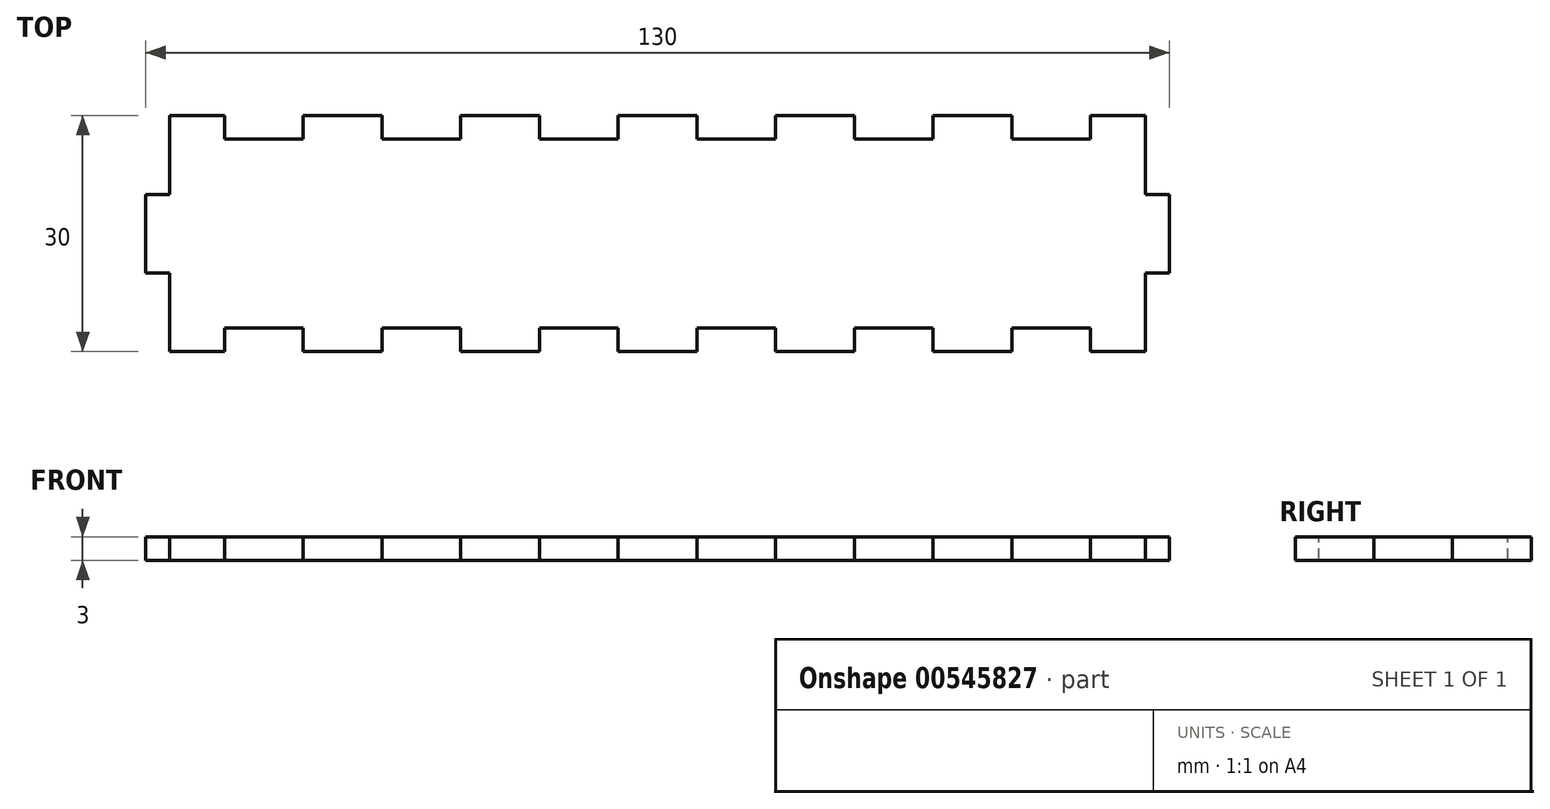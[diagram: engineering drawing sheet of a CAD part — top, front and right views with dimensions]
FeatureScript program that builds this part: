
annotation { "Feature Type Name" : "Feature", "Feature Type Description" : "" }
export const myFeature = defineFeature(function(context is Context, id is Id, definition is map)
    precondition{}
    {
        {
            var Q0;
            Q0=qCreatedBy(makeId("Top.planeOp"),FACE);
            var sketch = newSketch(context, id + "F0", { "sketchPlane" : qUnion([Q0])});
            skLineSegment(sketch, "E0.bottom", {"start": v(65, -15) * mm, "end": v(-65, -15) * mm});
            skLineSegment(sketch, "E0.top", {"start": v(65, 15) * mm, "end": v(-65, 15) * mm});
            skLineSegment(sketch, "E0.left", {"start": v(65, -15) * mm, "end": v(65, 15) * mm});
            skLineSegment(sketch, "E0.right", {"start": v(-65, -15) * mm, "end": v(-65, 15) * mm});
            skPoint(sketch, "E0.middle", {"position": v(0, 0) * mm});
            skSolve(sketch);
        }
        {
            var Q0;
            Q0=makeQuery(id+"F0.imprint","IMPRINT",FACE,{"disambiguationData":[TD([[makeQuery(id+"F0.imprint","IMPRINT",EDGE,{"derivedFrom":sQuery(id+"F0.wireOp",EDGE,"E0.bottom")}),-1.0]])]});
            var sketch = newSketch(context, id + "F1", { "sketchPlane" : qUnion([Q0])});
            skLineSegment(sketch, "E1.bottom", {"start": v(65, -15) * mm, "end": v(62, -15) * mm});
            skLineSegment(sketch, "E1.top", {"start": v(65, -5) * mm, "end": v(62, -5) * mm});
            skLineSegment(sketch, "E1.left", {"start": v(65, -15) * mm, "end": v(65, -5) * mm});
            skLineSegment(sketch, "E1.right", {"start": v(62, -15) * mm, "end": v(62, -5) * mm});
            skLineSegment(sketch, "E2.0.1.0", {"start": v(62, 5) * mm, "end": v(62, 15) * mm});
            skLineSegment(sketch, "E2.0.1.1", {"start": v(65, 5) * mm, "end": v(65, 15) * mm});
            skLineSegment(sketch, "E2.0.1.2", {"start": v(65, 15) * mm, "end": v(62, 15) * mm});
            skLineSegment(sketch, "E2.0.1.3", {"start": v(65, 5) * mm, "end": v(62, 5) * mm});
            skLineSegment(sketch, "E2.0.2.0", {"start": v(62, 25) * mm, "end": v(62, 35) * mm});
            skLineSegment(sketch, "E2.0.2.1", {"start": v(65, 25) * mm, "end": v(65, 35) * mm});
            skLineSegment(sketch, "E2.0.2.2", {"start": v(65, 35) * mm, "end": v(62, 35) * mm});
            skLineSegment(sketch, "E2.0.2.3", {"start": v(65, 25) * mm, "end": v(62, 25) * mm});
            skLineSegment(sketch, "E2.0.3.0", {"start": v(62, 45) * mm, "end": v(62, 55) * mm});
            skLineSegment(sketch, "E2.0.3.1", {"start": v(65, 45) * mm, "end": v(65, 55) * mm});
            skLineSegment(sketch, "E2.0.3.2", {"start": v(65, 55) * mm, "end": v(62, 55) * mm});
            skLineSegment(sketch, "E2.0.3.3", {"start": v(65, 45) * mm, "end": v(62, 45) * mm});
            skLineSegment(sketch, "E2.0.4.0", {"start": v(62, 65) * mm, "end": v(62, 75) * mm});
            skLineSegment(sketch, "E2.0.4.1", {"start": v(65, 65) * mm, "end": v(65, 75) * mm});
            skLineSegment(sketch, "E2.0.4.2", {"start": v(65, 75) * mm, "end": v(62, 75) * mm});
            skLineSegment(sketch, "E2.0.4.3", {"start": v(65, 65) * mm, "end": v(62, 65) * mm});
            skLineSegment(sketch, "E2.0.5.0", {"start": v(62, 85) * mm, "end": v(62, 95) * mm});
            skLineSegment(sketch, "E2.0.5.1", {"start": v(65, 85) * mm, "end": v(65, 95) * mm});
            skLineSegment(sketch, "E2.0.5.2", {"start": v(65, 95) * mm, "end": v(62, 95) * mm});
            skLineSegment(sketch, "E2.0.5.3", {"start": v(65, 85) * mm, "end": v(62, 85) * mm});
            skLineSegment(sketch, "E2.direction1", {"start": v(62, -15) * mm, "end": v(87, -15) * mm, "construction": true});
            skLineSegment(sketch, "E2.direction2", {"start": v(62, -15) * mm, "end": v(62, 5) * mm, "construction": true});
            skLineSegment(sketch, "E3", {"start": v(0, -56.46) * mm, "end": v(0, 57.33) * mm, "construction": true});
            skLineSegment(sketch, "E4.MirrorCS", {"start": v(-62, -15) * mm, "end": v(-62, 5) * mm, "construction": true});
            skLineSegment(sketch, "E5.MirrorCS", {"start": v(-62, -15) * mm, "end": v(-62, -5) * mm});
            skLineSegment(sketch, "E6.MirrorCS", {"start": v(-65, 65) * mm, "end": v(-65, 75) * mm});
            skLineSegment(sketch, "E7.MirrorCS", {"start": v(-62, 45) * mm, "end": v(-62, 55) * mm});
            skLineSegment(sketch, "E8.MirrorCS", {"start": v(-65, 25) * mm, "end": v(-62, 25) * mm});
            skLineSegment(sketch, "E9.MirrorCS", {"start": v(-65, 35) * mm, "end": v(-62, 35) * mm});
            skLineSegment(sketch, "E10.MirrorCS", {"start": v(-65, 65) * mm, "end": v(-62, 65) * mm});
            skLineSegment(sketch, "E11.MirrorCS", {"start": v(-65, 25) * mm, "end": v(-65, 35) * mm});
            skLineSegment(sketch, "E12.MirrorCS", {"start": v(-62, 25) * mm, "end": v(-62, 35) * mm});
            skLineSegment(sketch, "E13.MirrorCS", {"start": v(-65, 85) * mm, "end": v(-65, 95) * mm});
            skLineSegment(sketch, "E14.MirrorCS", {"start": v(-65, 5) * mm, "end": v(-62, 5) * mm});
            skLineSegment(sketch, "E15.MirrorCS", {"start": v(-65, 85) * mm, "end": v(-62, 85) * mm});
            skLineSegment(sketch, "E16.MirrorCS", {"start": v(-65, 95) * mm, "end": v(-62, 95) * mm});
            skLineSegment(sketch, "E17.MirrorCS", {"start": v(-62, 85) * mm, "end": v(-62, 95) * mm});
            skLineSegment(sketch, "E18.MirrorCS", {"start": v(-62, 65) * mm, "end": v(-62, 75) * mm});
            skLineSegment(sketch, "E19.MirrorCS", {"start": v(-65, 45) * mm, "end": v(-65, 55) * mm});
            skLineSegment(sketch, "E20.MirrorCS", {"start": v(-65, 55) * mm, "end": v(-62, 55) * mm});
            skLineSegment(sketch, "E21.MirrorCS", {"start": v(-65, 45) * mm, "end": v(-62, 45) * mm});
            skLineSegment(sketch, "E22.MirrorCS", {"start": v(-65, -15) * mm, "end": v(-62, -15) * mm});
            skLineSegment(sketch, "E23.MirrorCS", {"start": v(-65, -15) * mm, "end": v(-65, -5) * mm});
            skLineSegment(sketch, "E24.MirrorCS", {"start": v(-62, 5) * mm, "end": v(-62, 15) * mm});
            skLineSegment(sketch, "E25.MirrorCS", {"start": v(-65, 5) * mm, "end": v(-65, 15) * mm});
            skLineSegment(sketch, "E26.MirrorCS", {"start": v(-65, 15) * mm, "end": v(-62, 15) * mm});
            skLineSegment(sketch, "E27.MirrorCS", {"start": v(-65, 75) * mm, "end": v(-62, 75) * mm});
            skLineSegment(sketch, "E28.MirrorCS", {"start": v(-65, -5) * mm, "end": v(-62, -5) * mm});
            skSolve(sketch);
        }
        {
            var Q0;
            Q0=qSketchRegion(id+"F0",true);
            extrude(context, id + "F2", {"entities" : qUnion([Q0]), "depth" : 3 * mm, "offsetDistance" : 25 * mm});
        }
        {
            var Q0;
            Q0=qSketchRegion(id+"F1",true);
            extrude(context, id + "F3", {"entities" : qUnion([Q0]), "operationType" : NewBodyOperationType.REMOVE, "depth" : 25 * mm, "offsetDistance" : 25 * mm});
        }
        {
            var Q0;
            Q0=makeQuery(id+"F2.opExtrude","CAP_FACE",FACE,{"disambiguationData":[OSD([sQuery(id+"F0.wireOp",EDGE,"E0.bottom"),sQuery(id+"F0.wireOp",EDGE,"E0.top"),sQuery(id+"F0.wireOp",EDGE,"E0.left"),sQuery(id+"F0.wireOp",EDGE,"E0.right")])],"isStart":false});
            var sketch = newSketch(context, id + "F4", { "sketchPlane" : qUnion([Q0])});
            skPoint(sketch, "E29.firstSnap0", {"position": v(0, -15) * mm});
            skLineSegment(sketch, "E29.bottom", {"start": v(-55, -15) * mm, "end": v(-45, -15) * mm});
            skLineSegment(sketch, "E29.top", {"start": v(-55, -12) * mm, "end": v(-45, -12) * mm});
            skLineSegment(sketch, "E29.left", {"start": v(-55, -15) * mm, "end": v(-55, -12) * mm});
            skLineSegment(sketch, "E29.right", {"start": v(-45, -15) * mm, "end": v(-45, -12) * mm});
            skLineSegment(sketch, "E30.1.0.0", {"start": v(-35, -12) * mm, "end": v(-25, -12) * mm});
            skLineSegment(sketch, "E30.1.0.1", {"start": v(-35, -15) * mm, "end": v(-25, -15) * mm});
            skLineSegment(sketch, "E30.1.0.2", {"start": v(-25, -15) * mm, "end": v(-25, -12) * mm});
            skLineSegment(sketch, "E30.1.0.3", {"start": v(-35, -15) * mm, "end": v(-35, -12) * mm});
            skLineSegment(sketch, "E30.2.0.0", {"start": v(-15, -12) * mm, "end": v(-5, -12) * mm});
            skLineSegment(sketch, "E30.2.0.1", {"start": v(-15, -15) * mm, "end": v(-5, -15) * mm});
            skLineSegment(sketch, "E30.2.0.2", {"start": v(-5, -15) * mm, "end": v(-5, -12) * mm});
            skLineSegment(sketch, "E30.2.0.3", {"start": v(-15, -15) * mm, "end": v(-15, -12) * mm});
            skLineSegment(sketch, "E30.3.0.0", {"start": v(5, -12) * mm, "end": v(15, -12) * mm});
            skLineSegment(sketch, "E30.3.0.1", {"start": v(5, -15) * mm, "end": v(15, -15) * mm});
            skLineSegment(sketch, "E30.3.0.2", {"start": v(15, -15) * mm, "end": v(15, -12) * mm});
            skLineSegment(sketch, "E30.3.0.3", {"start": v(5, -15) * mm, "end": v(5, -12) * mm});
            skLineSegment(sketch, "E30.4.0.0", {"start": v(25, -12) * mm, "end": v(35, -12) * mm});
            skLineSegment(sketch, "E30.4.0.1", {"start": v(25, -15) * mm, "end": v(35, -15) * mm});
            skLineSegment(sketch, "E30.4.0.2", {"start": v(35, -15) * mm, "end": v(35, -12) * mm});
            skLineSegment(sketch, "E30.4.0.3", {"start": v(25, -15) * mm, "end": v(25, -12) * mm});
            skLineSegment(sketch, "E30.5.0.0", {"start": v(45, -12) * mm, "end": v(55, -12) * mm});
            skLineSegment(sketch, "E30.5.0.1", {"start": v(45, -15) * mm, "end": v(55, -15) * mm});
            skLineSegment(sketch, "E30.5.0.2", {"start": v(55, -15) * mm, "end": v(55, -12) * mm});
            skLineSegment(sketch, "E30.5.0.3", {"start": v(45, -15) * mm, "end": v(45, -12) * mm});
            skLineSegment(sketch, "E30.direction1", {"start": v(-55, -12) * mm, "end": v(-35, -12) * mm, "construction": true});
            skLineSegment(sketch, "E31", {"start": v(53.33, 0) * mm, "end": v(63.5, 0) * mm, "construction": true});
            skPoint(sketch, "E31.startSnap0", {"position": v(63.5, -5) * mm});
            skLineSegment(sketch, "E32.MirrorCS", {"start": v(-55, 12) * mm, "end": v(-35, 12) * mm, "construction": true});
            skLineSegment(sketch, "E33.MirrorCS", {"start": v(35, 15) * mm, "end": v(35, 12) * mm});
            skLineSegment(sketch, "E34.MirrorCS", {"start": v(-55, 15) * mm, "end": v(-55, 12) * mm});
            skLineSegment(sketch, "E35.MirrorCS", {"start": v(55, 15) * mm, "end": v(55, 12) * mm});
            skLineSegment(sketch, "E36.MirrorCS", {"start": v(-25, 15) * mm, "end": v(-25, 12) * mm});
            skLineSegment(sketch, "E37.MirrorCS", {"start": v(25, 15) * mm, "end": v(25, 12) * mm});
            skLineSegment(sketch, "E38.MirrorCS", {"start": v(75, 15) * mm, "end": v(75, 12) * mm});
            skLineSegment(sketch, "E39.MirrorCS", {"start": v(-15, 15) * mm, "end": v(-15, 12) * mm});
            skLineSegment(sketch, "E40.MirrorCS", {"start": v(65, 15) * mm, "end": v(65, 12) * mm});
            skLineSegment(sketch, "E41.MirrorCS", {"start": v(-5, 15) * mm, "end": v(-5, 12) * mm});
            skLineSegment(sketch, "E42.MirrorCS", {"start": v(-35, 15) * mm, "end": v(-35, 12) * mm});
            skLineSegment(sketch, "E43.MirrorCS", {"start": v(15, 15) * mm, "end": v(15, 12) * mm});
            skLineSegment(sketch, "E44.MirrorCS", {"start": v(45, 15) * mm, "end": v(45, 12) * mm});
            skLineSegment(sketch, "E45.MirrorCS", {"start": v(-45, 15) * mm, "end": v(-45, 12) * mm});
            skLineSegment(sketch, "E46.MirrorCS", {"start": v(5, 15) * mm, "end": v(5, 12) * mm});
            skLineSegment(sketch, "E47.MirrorCS", {"start": v(-55, 12) * mm, "end": v(-45, 12) * mm});
            skLineSegment(sketch, "E48.MirrorCS", {"start": v(65, 15) * mm, "end": v(75, 15) * mm});
            skLineSegment(sketch, "E49.MirrorCS", {"start": v(25, 12) * mm, "end": v(35, 12) * mm});
            skLineSegment(sketch, "E50.MirrorCS", {"start": v(45, 12) * mm, "end": v(55, 12) * mm});
            skLineSegment(sketch, "E51.MirrorCS", {"start": v(45, 15) * mm, "end": v(55, 15) * mm});
            skLineSegment(sketch, "E52.MirrorCS", {"start": v(65, 12) * mm, "end": v(75, 12) * mm});
            skLineSegment(sketch, "E53.MirrorCS", {"start": v(5, 12) * mm, "end": v(15, 12) * mm});
            skLineSegment(sketch, "E54.MirrorCS", {"start": v(-55, 15) * mm, "end": v(-45, 15) * mm});
            skLineSegment(sketch, "E55.MirrorCS", {"start": v(-15, 12) * mm, "end": v(-5, 12) * mm});
            skLineSegment(sketch, "E56.MirrorCS", {"start": v(-15, 15) * mm, "end": v(-5, 15) * mm});
            skLineSegment(sketch, "E57.MirrorCS", {"start": v(-35, 15) * mm, "end": v(-25, 15) * mm});
            skLineSegment(sketch, "E58.MirrorCS", {"start": v(5, 15) * mm, "end": v(15, 15) * mm});
            skLineSegment(sketch, "E59.MirrorCS", {"start": v(25, 15) * mm, "end": v(35, 15) * mm});
            skPoint(sketch, "E60.MirrorP", {"position": v(0, 15) * mm});
            skLineSegment(sketch, "E61.MirrorCS", {"start": v(-35, 12) * mm, "end": v(-25, 12) * mm});
            skSolve(sketch);
        }
        {
            var Q0;
            Q0=qSketchRegion(id+"F4",true);
            extrude(context, id + "F5", {"entities" : qUnion([Q0]), "operationType" : NewBodyOperationType.REMOVE, "oppositeDirection" : true, "depth" : 25 * mm, "offsetDistance" : 25 * mm});
        }
    });
